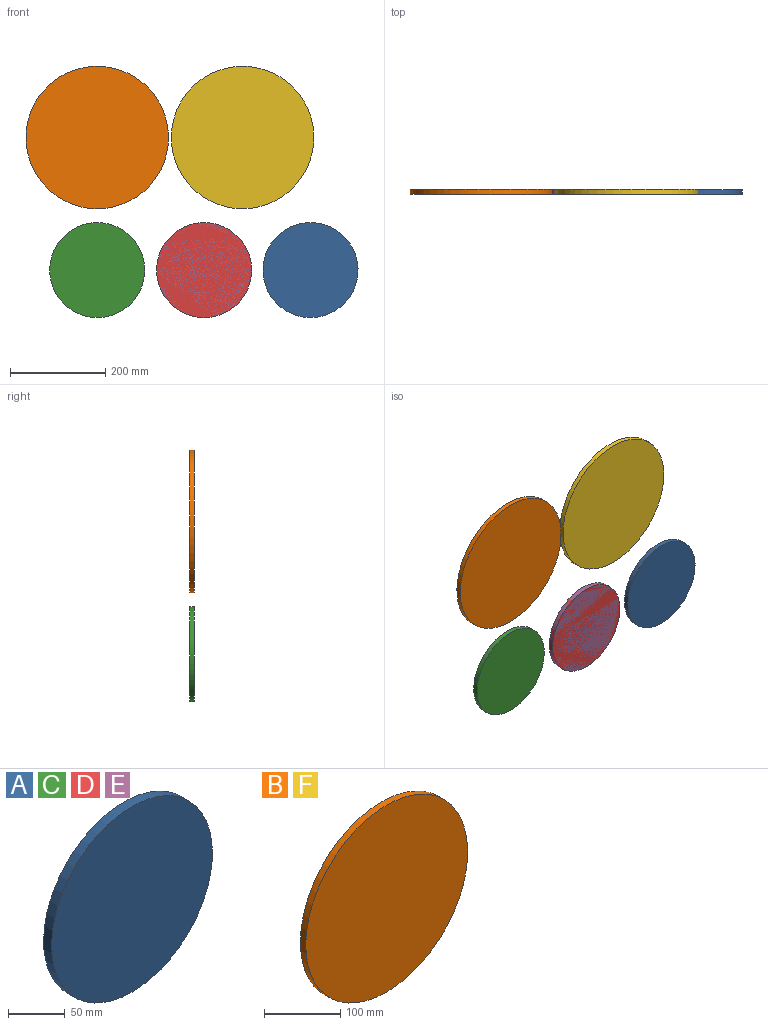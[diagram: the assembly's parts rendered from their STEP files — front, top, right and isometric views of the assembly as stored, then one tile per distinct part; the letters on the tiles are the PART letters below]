
ASSEMBLY  parts=6 mates=5
PART A: 3 faces, bbox 200x10x200 mm
  f0: cylinder r=100mm len=200mm, axis (0,1,0), area 6283.2mm2, adj f1,f2
  f1: plane 200x200mm, normal (0,-1,0), area 31415.9mm2, adj f0
  f2: plane 200x200mm, normal (0,1,0), area 31415.9mm2, adj f0
PART B: 3 faces, bbox 300x10x300 mm
  f0: cylinder r=150mm len=300mm, axis (0,1,0), area 9424.8mm2, adj f1,f2
  f1: plane 300x300mm, normal (0,-1,0), area 70685.8mm2, adj f0
  f2: plane 300x300mm, normal (0,1,0), area 70685.8mm2, adj f0
PART C: same geometry as A
PART D: same geometry as A
PART E: same geometry as A
PART F: same geometry as B
PLACE A t=(56.81,5,-113.83)mm
PLACE B t=(-392.19,5,165.17)mm
PLACE C t=(-392.19,5,-113.83)mm
PLACE D t=(-167.19,5,-113.83)mm
PLACE E t=(-167.19,5,-113.83)mm
PLACE F t=(-86.19,5,165.17)mm
MATE parallel C.f0 <-> D.f0  axis (0,-1,0) through (-392.19,-5,-113.83)mm
MATE parallel E.f0 <-> D.f0  axis (0,-1,0) through (-167.19,-5,-113.83)mm
MATE parallel D.f0 <-> B.f0  axis (0,-1,0) through (-167.19,-5,-113.83)mm
MATE parallel A.f0 <-> C.f0  axis (0,-1,0) through (56.81,-5,-113.83)mm
MATE parallel B.f0 <-> F.f0  axis (0,-1,0) through (-392.19,-5,165.17)mm
